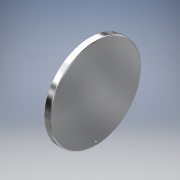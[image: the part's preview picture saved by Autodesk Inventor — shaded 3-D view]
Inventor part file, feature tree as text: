
AUTODESK INVENTOR PART (.ipt)
format: ipt  version: 2019 (Build 230136000, 136)  size: 142,848 bytes
history: native  units: in
note: dims shown in document units (in); Inventor stores cm internally (conversion verified against a paired STEP export)
features: sketch x3, hole x2, revolve x1, fillet x1, chamfer x1, projected_geometry x1
ambient origin geometry x8: Origin, YZ Plane, XZ Plane, XY Plane, X Axis, Y Axis, Z Axis, Center Point
bodies: Body1 (feature_tree)
feature tree (9):
  revolve  "Revolution1"  [1 undecoded]
  fillet  "Fillet1"  Radius=0.25in
  chamfer  "Chamfer1"  Distance=0.025in
  hole  "Hole1"  [1 undecoded]
  hole  "Hole2"  [1 undecoded]
  sketch  "Sketch5"  dims[d9=0.125in d10=1.875in d14=0.25in]
  sketch  "Sketch6"  dims[d15=90.0deg]
  projected_geometry  "Projected Loop2"
  sketch  "Sketch7"  dims[d17=0.05in d18=0.025in d19=0.165in d21=0.225in d22=0.025in d23=0.125in d24=45.0deg d27=1.7in d29=0.06in d30=0.75in d31=0.375in d32=0.25in d33=0.5635in d34=1.0in d35=0.8108in d36=0.104in d37=0.276in d38=0.375in d39=0.25in d40=0.5635in d41=0.432in d42=0.8108in d43=2.75in d44=0.75in]
note: 3 required parameter values undecoded (feature->parameter linkage not recoverable at this tier; creation-order binding heuristic only, values carry confidence <= 0.55)